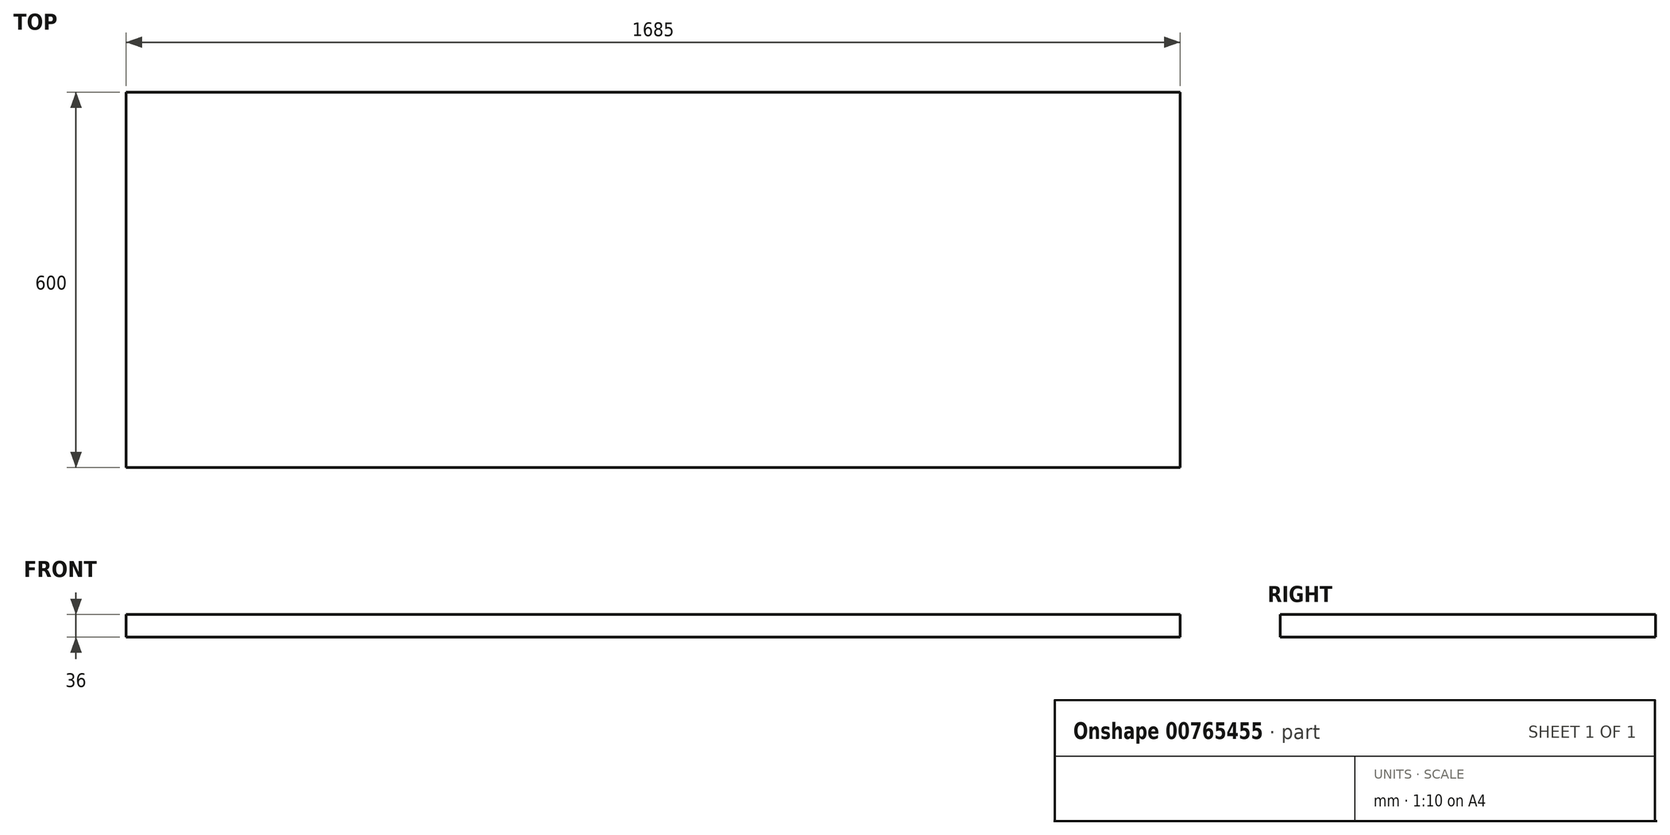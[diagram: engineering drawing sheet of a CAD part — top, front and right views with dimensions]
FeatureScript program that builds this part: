
annotation { "Feature Type Name" : "Feature", "Feature Type Description" : "" }
export const myFeature = defineFeature(function(context is Context, id is Id, definition is map)
    precondition{}
    {
        {
            var Q0;
            Q0=qCreatedBy(makeId("Top.planeOp"),FACE);
            var sketch = newSketch(context, id + "F0", { "sketchPlane" : qUnion([Q0])});
            skLineSegment(sketch, "E0.bottom", {"start": v(-842.5, -300) * mm, "end": v(842.5, -300) * mm});
            skLineSegment(sketch, "E0.top", {"start": v(-842.5, 300) * mm, "end": v(842.5, 300) * mm});
            skLineSegment(sketch, "E0.left", {"start": v(-842.5, -300) * mm, "end": v(-842.5, 300) * mm});
            skLineSegment(sketch, "E0.right", {"start": v(842.5, -300) * mm, "end": v(842.5, 300) * mm});
            skPoint(sketch, "E0.middle", {"position": v(0, 0) * mm});
            skSolve(sketch);
        }
        {
            var Q0;
            Q0 = qSketchRegion(id + "F0", true);
            extrude(context, id + "F1", {"entities" : qUnion([Q0]), "depth" : 36 * mm, "offsetDistance" : 25 * mm});
        }
    });
